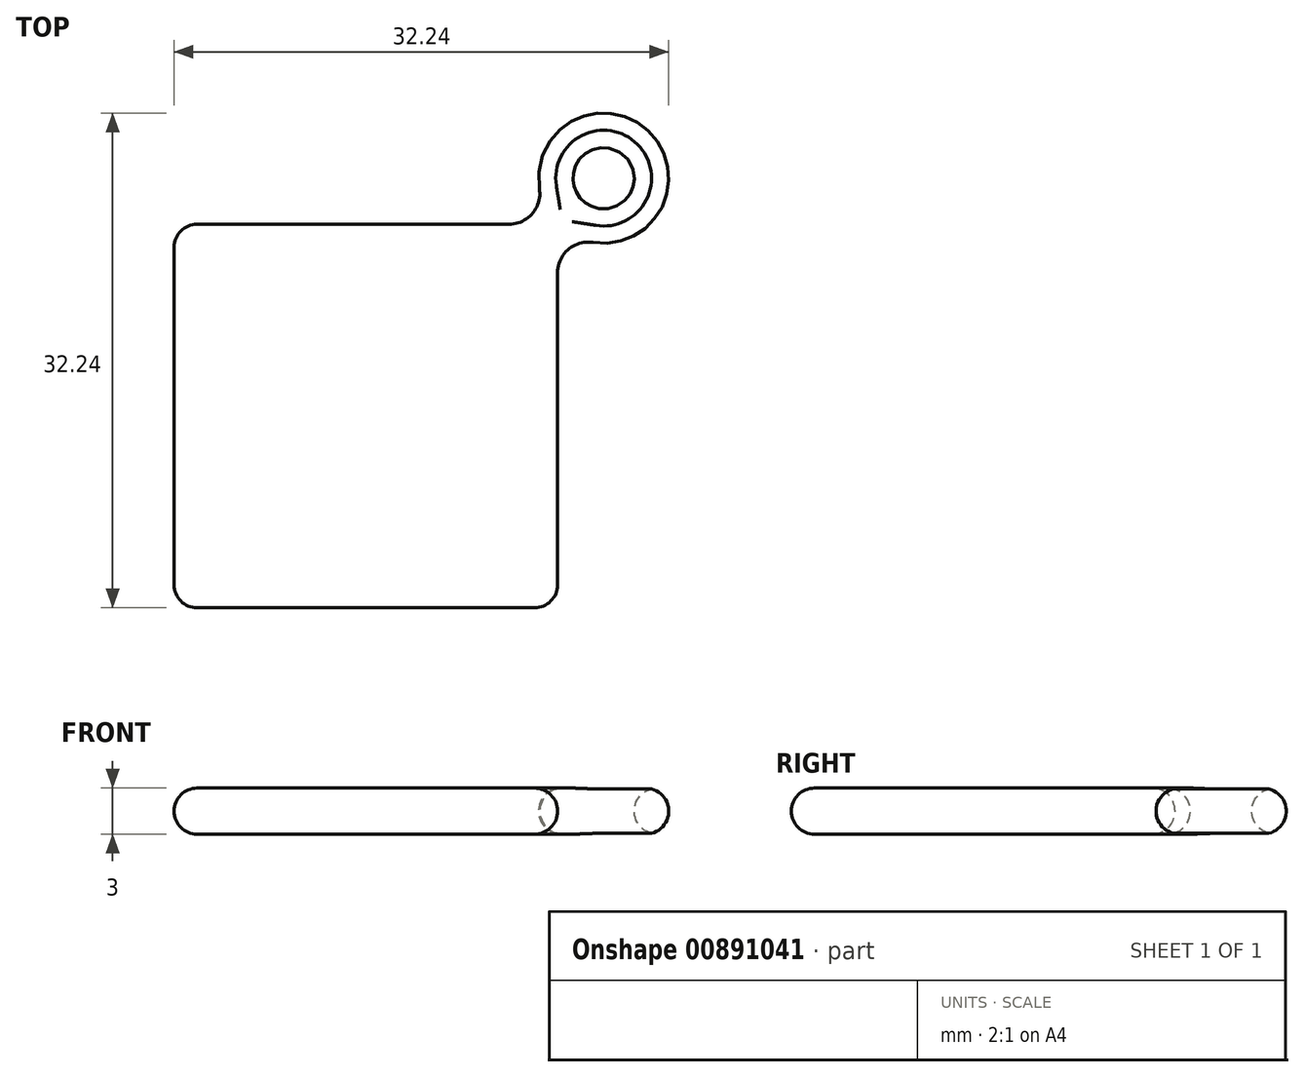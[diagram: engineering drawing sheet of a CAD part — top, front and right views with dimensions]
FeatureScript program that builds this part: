
annotation { "Feature Type Name" : "Feature", "Feature Type Description" : "" }
export const myFeature = defineFeature(function(context is Context, id is Id, definition is map)
    precondition{}
    {
        {
            var Q0;
            Q0=qCreatedBy(makeId("Top.planeOp"),FACE);
            var sketch = newSketch(context, id + "F0", { "sketchPlane" : qUnion([Q0])});
            skLineSegment(sketch, "E0.bottom", {"start": v(0, 0) * mm, "end": v(25, 0) * mm});
            skLineSegment(sketch, "E0.top", {"start": v(0, 25) * mm, "end": v(21.84, 25) * mm});
            skLineSegment(sketch, "E0.left", {"start": v(0, 0) * mm, "end": v(0, 25) * mm});
            skLineSegment(sketch, "E0.right", {"start": v(25, 0) * mm, "end": v(25, 21.84) * mm});
            skLineSegment(sketch, "E1", {"start": v(25, 25) * mm, "end": v(25, 28) * mm, "construction": true});
            skLineSegment(sketch, "E2", {"start": v(25, 25) * mm, "end": v(28, 25) * mm, "construction": true});
            skLineSegment(sketch, "E3", {"start": v(25, 28) * mm, "end": v(28, 28) * mm, "construction": true});
            skLineSegment(sketch, "E4", {"start": v(28, 28) * mm, "end": v(28, 25) * mm, "construction": true});
            skCircle(sketch, "E5", {"center": v(28, 28) * mm, "radius": 2 * mm});
            skLineSegment(sketch, "E6", {"start": v(25, 25) * mm, "end": v(31, 31) * mm, "construction": true});
            skArc(sketch, "E7", {"start": v(31, 31) * mm, "mid": v(26.07, 31.78) * mm, "end": v(23.81, 27.32) * mm});
            skArc(sketch, "E8", {"start": v(27.32, 23.81) * mm, "mid": v(31.78, 26.07) * mm, "end": v(31, 31) * mm});
            skPoint(sketch, "E9.visualSharp", {"position": v(25, 25) * mm});
            skArc(sketch, "E9.filletArc", {"start": v(21.84, 25) * mm, "mid": v(23.36, 25.7) * mm, "end": v(23.81, 27.32) * mm});
            skArc(sketch, "E10.filletArc", {"start": v(27.32, 23.81) * mm, "mid": v(25.7, 23.36) * mm, "end": v(25, 21.84) * mm});
            skSolve(sketch);
        }
        {
            var Q0;
            Q0 = qSketchRegion(id + "F0", true);
            extrude(context, id + "F1", {"entities" : qUnion([Q0]), "depth" : 3 * mm, "offsetDistance" : 25 * mm});
        }
        {
            var Q0;
            Q0=makeQuery(id+"F1.opExtrude","CAP_FACE",FACE,{"disambiguationData":[OSD([sQuery(id+"F0.wireOp",EDGE,"E0.bottom"),sQuery(id+"F0.wireOp",EDGE,"E0.top"),sQuery(id+"F0.wireOp",EDGE,"E0.left"),sQuery(id+"F0.wireOp",EDGE,"E0.right"),sQuery(id+"F0.wireOp",EDGE,"E5"),sQuery(id+"F0.wireOp",EDGE,"E7"),sQuery(id+"F0.wireOp",EDGE,"E8"),sQuery(id+"F0.wireOp",EDGE,"E9.filletArc"),sQuery(id+"F0.wireOp",EDGE,"E10.filletArc")])],"isStart":false});
            var Q1;
            Q1=makeQuery(id+"F1.opExtrude","CAP_FACE",FACE,{"disambiguationData":[OSD([sQuery(id+"F0.wireOp",EDGE,"E0.bottom"),sQuery(id+"F0.wireOp",EDGE,"E0.top"),sQuery(id+"F0.wireOp",EDGE,"E0.left"),sQuery(id+"F0.wireOp",EDGE,"E0.right"),sQuery(id+"F0.wireOp",EDGE,"E5"),sQuery(id+"F0.wireOp",EDGE,"E7"),sQuery(id+"F0.wireOp",EDGE,"E8"),sQuery(id+"F0.wireOp",EDGE,"E9.filletArc"),sQuery(id+"F0.wireOp",EDGE,"E10.filletArc")])],"isStart":true});
            var Q2;
            Q2=makeQuery(id+"F1.opExtrude","SWEPT_EDGE",EDGE,{"disambiguationData":[OSD([sQuery(id+"F0.wireOp",EDGE,"E0.bottom"),sQuery(id+"F0.wireOp",EDGE,"E0.right")])]});
            var Q3;
            Q3=makeQuery(id+"F1.opExtrude","SWEPT_EDGE",EDGE,{"disambiguationData":[OSD([sQuery(id+"F0.wireOp",EDGE,"E0.bottom"),sQuery(id+"F0.wireOp",EDGE,"E0.left")])]});
            var Q4;
            Q4=makeQuery(id+"F1.opExtrude","SWEPT_EDGE",EDGE,{"disambiguationData":[OSD([sQuery(id+"F0.wireOp",EDGE,"E0.top"),sQuery(id+"F0.wireOp",EDGE,"E0.left")])]});
            fillet(context, id + "F2", {"entities" : qUnion([Q0, Q1, Q2, Q3, Q4]), "radius" : 1.5 * mm, "tangentPropagation" : true, "allowEdgeOverflow" : false});
        }
    });
